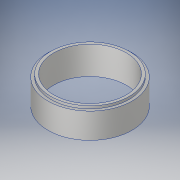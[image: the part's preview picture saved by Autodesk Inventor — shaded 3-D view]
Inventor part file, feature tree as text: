
AUTODESK INVENTOR PART (.ipt)
format: ipt  version: 2017 SP1 (Build 210196100, 196)  size: 153,088 bytes
history: native  units: in
note: dims shown in document units (in); Inventor stores cm internally (conversion verified against a paired STEP export)
features: revolve x1, sketch x1
ambient origin geometry x8: Origin, YZ Plane, XZ Plane, XY Plane, X Axis, Y Axis, Z Axis, Center Point
bodies: Solid1 (feature_tree)
feature tree (2):
  revolve  "Revolution1"  [1 undecoded]
  sketch  "Sketch1"  dims[d0=1.13in d1=3.75in d2=0.125in d3=0.1718in d5=1.0in d6=1.0in d7=90.0deg d8=0.5in d9=15.0deg d12=1.25in d13=0.25in d16=0.5in d17=0.5in d18=0.5in d19=2.5in d20=0.5in d22=0.375in d23=0.25in d25=0.234in d27=0.125in d28=0.25in d29=1.0in d30=4.25in d31=0.25in d33=0.8014in d34=15.0deg d35=0.125in d36=1.0in d37=90.0deg]
note: 1 required parameter value undecoded (feature->parameter linkage not recoverable at this tier; creation-order binding heuristic only, values carry confidence <= 0.55)
